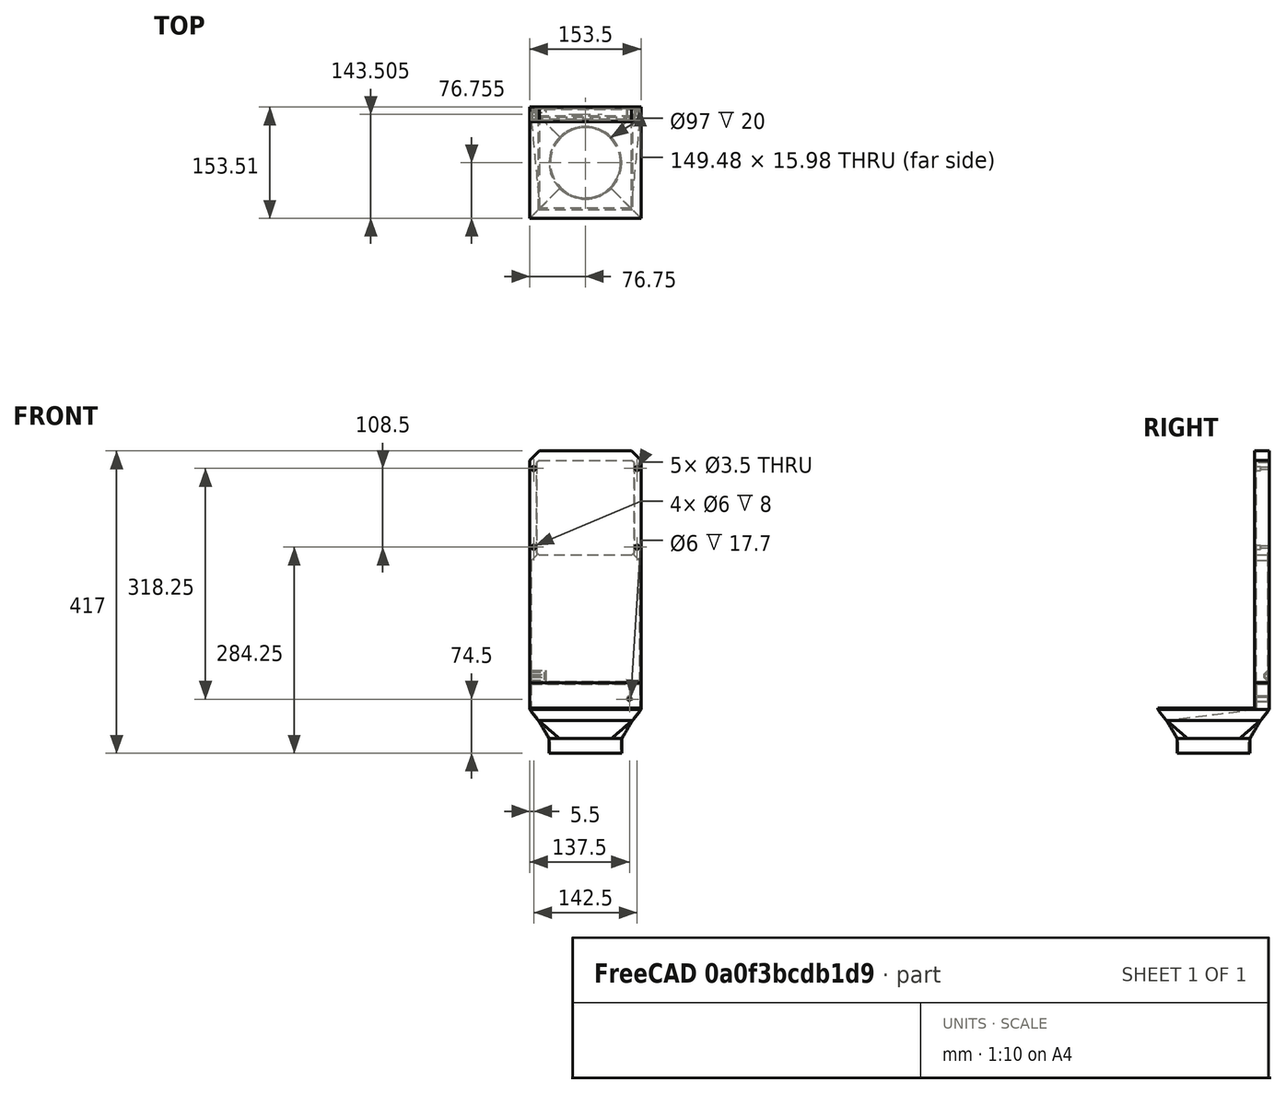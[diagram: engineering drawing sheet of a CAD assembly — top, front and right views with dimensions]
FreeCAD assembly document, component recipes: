
FREECAD ASSEMBLY — COMPONENT RECIPES ("H2C Vertical Exhaust")

This assembly document has 2 components, labeled P0..P1 below (a component is one placed body or linked part). 2 of them carry a construction recipe — the FreeCAD feature program that regenerates the part from scratch, quoted from this document or its linked companion documents; the rest are supplied as boundary geometry only. No exploded tour is included for this assembly.
COMPONENT P0 — recipe-attached ("Back of printer001", modeled in this document).
Construction recipe (the document's own serialized feature program — sketch geometry with constraints, then the solid features built on it; lengths are millimeters unless a unit is written):

FEATURE [Sketcher::SketchObject] Sketch
  ArcFitTolerance = 1e-06
  AttachmentSupport = -> [XZ_Plane]
  ExternalTypes = [0]
  FullyConstrained = true
  MakeInternals = false
  MapMode = 5
  Placement = pos=(0,0,0) rot=(1,0,0;1.5708rad)
  sketch-geometry (25):
    g0: LineSegment StartX=-76.75 StartY=-241.5 StartZ=0 EndX=76.75 EndY=-241.5 EndZ=0
    g1: LineSegment StartX=76.75 StartY=-241.5 StartZ=0 EndX=76.75 EndY=65.5 EndZ=0
    g2: LineSegment StartX=63.75 StartY=78.5 StartZ=0 EndX=-63.75 EndY=78.5 EndZ=0
    g3: LineSegment StartX=-76.75 StartY=65.5 StartZ=0 EndX=-76.75 EndY=-241.5 EndZ=0
    g4: GeomPoint X=0 Y=0 Z=0
    g5: GeomPoint X=-76.75 Y=78.5 Z=0
    g6: GeomPoint X=76.75 Y=78.5 Z=0
    g7: LineSegment StartX=-63.75 StartY=-65.5 StartZ=0 EndX=63.75 EndY=-65.5 EndZ=0
    g8: LineSegment StartX=67.25 StartY=-62 StartZ=0 EndX=67.25 EndY=62 EndZ=0
    g9: LineSegment StartX=63.75 StartY=65.5 StartZ=0 EndX=-63.75 EndY=65.5 EndZ=0
    g10: LineSegment StartX=-67.25 StartY=62 StartZ=0 EndX=-67.25 EndY=-62 EndZ=0
    g11: GeomPoint X=0 Y=0 Z=0
    g12: GeomPoint X=-67.25 Y=65.5 Z=0
    g13: GeomPoint X=67.25 Y=65.5 Z=0
    g14: GeomPoint X=67.25 Y=-62 Z=0
    g15: Circle CenterX=-71.25 CenterY=54.25 CenterZ=0 NormalX=0 NormalY=0 NormalZ=1 AngleXU=0 Radius=1.75
    g16: Circle CenterX=71.25 CenterY=54.25 CenterZ=0 NormalX=0 NormalY=0 NormalZ=1 AngleXU=0 Radius=1.75
    g17: Circle CenterX=71.25 CenterY=-54.25 CenterZ=0 NormalX=0 NormalY=0 NormalZ=1 AngleXU=0 Radius=1.75
    g18: Circle CenterX=-71.25 CenterY=-54.25 CenterZ=0 NormalX=0 NormalY=0 NormalZ=1 AngleXU=0 Radius=1.75
    g19: LineSegment StartX=-76.75 StartY=65.5 StartZ=0 EndX=-63.75 EndY=78.5 EndZ=0
    g20: LineSegment StartX=63.75 StartY=78.5 StartZ=0 EndX=76.75 EndY=65.5 EndZ=0
    g21: LineSegment StartX=-67.25 StartY=62 StartZ=0 EndX=-63.75 EndY=65.5 EndZ=0
    g22: LineSegment StartX=63.75 StartY=65.5 StartZ=0 EndX=67.25 EndY=62 EndZ=0
    g23: LineSegment StartX=-67.25 StartY=-62 StartZ=0 EndX=-63.75 EndY=-65.5 EndZ=0
    g24: LineSegment StartX=63.75 StartY=-65.5 StartZ=0 EndX=67.25 EndY=-62 EndZ=0
  constraints (59):
    c: Horizontal(g0)
    c: Vertical(g3)
    c: Coincident(g4,g-1)
    c: DistanceX(g5,g6) = 153.5
    c: PointOnObject(g5,g3)
    c: PointOnObject(g5,g2)
    c: PointOnObject(g6,g2)
    c: PointOnObject(g6,g1)
    c: Horizontal(g7)
    c: Coincident(g11,g4)
    c: DistanceX(g12,g13) = 134.5
    c: DistanceY(g14,g13) = 127.5
    c: PointOnObject(g12,g10)
    c: PointOnObject(g12,g9)
    c: PointOnObject(g13,g9)
    c: PointOnObject(g13,g8)
    c: Horizontal(g15,g16)
    c: Horizontal(g18,g17)
    c: Vertical(g16,g17)
    c: Vertical(g15,g18)
    c: DistanceX(g15,g16) = 142.5
    c: DistanceY(g17,g16) = 108.5
    c: Symmetric(g18,g16,g4)
    c: Equal(g15,g16)
    c: Equal(g15,g18)
    c: Equal(g15,g17)
    c: Diameter(g15) = 3.5
    c: Vertical(g10)
    c: Coincident(g14,g8)
    c: Coincident(g1,g0)
    c: Coincident(g0,g3)
    c: DistanceY(g0,g2) = 320
    c: Coincident(g19,g3)
    c: Coincident(g19,g2)
    c: Coincident(g20,g2)
    c: Coincident(g20,g1)
    c: Symmetric(g2,g2,g-2)
    c: Symmetric(g3,g1,g-2)
    c: DistanceX(g3,g9) = 13
    c: Horizontal(g3,g9)
    c: Vertical(g2,g9)
    c: Coincident(g21,g10)
    c: Coincident(g21,g9)
    c: Coincident(g22,g9)
    c: Coincident(g22,g8)
    c: Angle(g19,g3) = 0.785398
    c: Angle(g21,g10) = 0.785398
    c: Symmetric(g9,g9,g-2)
    c: Symmetric(g8,g10,g-2)
    c: Vertical(g7,g9)
    c: Coincident(g23,g10)
    c: Coincident(g23,g7)
    c: Coincident(g24,g7)
    c: Coincident(g24,g8)
    c: Vertical(g7,g9)
    c: Horizontal(g10,g8)
    c: Angle(g10,g23) = 0.785398
    c: Symmetric(g8,g10,g4)
    c: Vertical(g1)
FEATURE [PartDesign::Pad] Pad  label="Surface against printer"
  Direction = (0,-1,2e-16)
  Length = 2
  Length2 = 10
  Placement = pos=(0,0,0) rot=(1,0,0;1.5708rad)
  Profile = -> Sketch
  ReferenceAxis = -> Sketch [N_Axis]
  SideType = 0
  Suppressed = false
  Type = 0
  Type2 = 0
FEATURE [Sketcher::SketchObject] Sketch011
  ArcFitTolerance = 1e-06
  AttachmentSupport = -> [Pad]
  ExternalGeometry = -> [Pad]
  ExternalTypes = [0]
  FullyConstrained = true
  MakeInternals = false
  MapMode = 5
  Placement = pos=(0,-1.17e-14,0) rot=(-1,0,0;1.5708rad)
  sketch-geometry (16):
    g0: LineSegment StartX=-76.75 StartY=-65.5 StartZ=0 EndX=-76.75 EndY=241.5 EndZ=0
    g1: LineSegment StartX=-76.75 StartY=241.5 StartZ=0 EndX=-74.75 EndY=241.5 EndZ=0
    g2: LineSegment StartX=-74.75 StartY=241.5 StartZ=0 EndX=-74.75 EndY=73 EndZ=0
    g3: LineSegment StartX=-74.75 StartY=73 StartZ=0 EndX=-67.25 EndY=65.5 EndZ=0
    g4: LineSegment StartX=-67.25 StartY=65.5 StartZ=0 EndX=-67.25 EndY=-62 EndZ=0
    g5: LineSegment StartX=-67.25 StartY=-62 StartZ=0 EndX=-63.75 EndY=-65.5 EndZ=0
    g6: LineSegment StartX=-63.75 StartY=-65.5 StartZ=0 EndX=63.75 EndY=-65.5 EndZ=0
    g7: LineSegment StartX=63.75 StartY=-65.5 StartZ=0 EndX=67.25 EndY=-62 EndZ=0
    g8: LineSegment StartX=67.25 StartY=-62 StartZ=0 EndX=67.25 EndY=65.5 EndZ=0
    g9: LineSegment StartX=67.25 StartY=65.5 StartZ=0 EndX=74.75 EndY=73 EndZ=0
    g10: LineSegment StartX=74.75 StartY=73 StartZ=0 EndX=74.75 EndY=241.5 EndZ=0
    g11: LineSegment StartX=74.75 StartY=241.5 StartZ=0 EndX=76.75 EndY=241.5 EndZ=0
    g12: LineSegment StartX=76.75 StartY=241.5 StartZ=0 EndX=76.75 EndY=-65.5 EndZ=0
    g13: LineSegment StartX=76.75 StartY=-65.5 StartZ=0 EndX=63.75 EndY=-78.5 EndZ=0
    g14: LineSegment StartX=63.75 StartY=-78.5 StartZ=0 EndX=-63.75 EndY=-78.5 EndZ=0
    g15: LineSegment StartX=-63.75 StartY=-78.5 StartZ=0 EndX=-76.75 EndY=-65.5 EndZ=0
  constraints (38):
    c: Coincident(g-6,g0)
    c: Coincident(g0,g-7)
    c: Coincident(g0,g1)
    c: PointOnObject(g1,g-7)
    c: Coincident(g1,g2)
    c: Vertical(g2)
    c: Coincident(g2,g3)
    c: Coincident(g3,g4)
    c: Coincident(g4,g-3)
    c: PointOnObject(g-3,g4)
    c: DistanceX(g1,g1) = 2
    c: Angle(g2,g3) = 0.785398
    c: PointOnObject(g3,g-8)
    c: Coincident(g4,g5)
    c: Coincident(g5,g-9)
    c: Coincident(g5,g6)
    c: Coincident(g6,g-9)
    c: Coincident(g6,g7)
    c: Coincident(g7,g-4)
    c: Coincident(g7,g8)
    c: Vertical(g8)
    c: Coincident(g8,g9)
    c: Coincident(g9,g10)
    c: PointOnObject(g10,g-7)
    c: Vertical(g10)
    c: Coincident(g10,g11)
    c: Coincident(g11,g-7)
    c: Coincident(g11,g12)
    c: Coincident(g12,g-5)
    c: Coincident(g12,g13)
    c: Coincident(g13,g-5)
    c: Coincident(g13,g14)
    c: Coincident(g14,g-6)
    c: Coincident(g14,g15)
    c: Coincident(g15,g0)
    c: Angle(g9,g10) = 0.785398
    c: PointOnObject(g8,g-8)
    c: Equal(g11,g1)
FEATURE [PartDesign::Pad] Pad006  label="Duct walls"
  BaseFeature = -> Pad
  Direction = (0,1,2e-16)
  Length = 16
  Length2 = 10
  Placement = pos=(0,0,0) rot=(1,0,0;1.5708rad)
  Profile = -> Sketch011
  ReferenceAxis = -> Sketch011 [N_Axis]
  Refine = true
  SideType = 0
  Suppressed = false
  Type = 0
  Type2 = 0
FEATURE [Sketcher::SketchObject] Sketch012
  ArcFitTolerance = 1e-06
  AttachmentSupport = -> [Pad006]
  ExternalGeometry = -> [Pad006]
  ExternalTypes = [0]
  FullyConstrained = true
  MakeInternals = false
  MapMode = 5
  Placement = pos=(0,16,0) rot=(-1,0,0;1.5708rad)
  sketch-geometry (6):
    g0: LineSegment StartX=-76.75 StartY=241.5 StartZ=0 EndX=-76.75 EndY=-65.5 EndZ=0
    g1: LineSegment StartX=-76.75 StartY=-65.5 StartZ=0 EndX=-63.75 EndY=-78.5 EndZ=0
    g2: LineSegment StartX=-63.75 StartY=-78.5 StartZ=0 EndX=63.75 EndY=-78.5 EndZ=0
    g3: LineSegment StartX=63.75 StartY=-78.5 StartZ=0 EndX=76.75 EndY=-65.5 EndZ=0
    g4: LineSegment StartX=76.75 StartY=-65.5 StartZ=0 EndX=76.75 EndY=241.5 EndZ=0
    g5: LineSegment StartX=76.75 StartY=241.5 StartZ=0 EndX=-76.75 EndY=241.5 EndZ=0
  constraints (12):
    c: Coincident(g-3,g0)
    c: Coincident(g0,g-3)
    c: Coincident(g0,g1)
    c: Coincident(g1,g-5)
    c: Coincident(g1,g2)
    c: Coincident(g2,g-5)
    c: Coincident(g2,g3)
    c: Coincident(g3,g-4)
    c: Coincident(g3,g4)
    c: Coincident(g4,g-4)
    c: Coincident(g4,g5)
    c: Coincident(g5,g0)
FEATURE [PartDesign::Pad] Pad007  label="Surface away from printer"
  BaseFeature = -> Pad006
  Direction = (0,1,2e-16)
  Length = 2
  Length2 = 10
  Placement = pos=(0,0,0) rot=(1,0,0;1.5708rad)
  Profile = -> Sketch012
  ReferenceAxis = -> Sketch012 [N_Axis]
  Refine = true
  SideType = 0
  Suppressed = false
  Type = 0
  Type2 = 0
FEATURE [Sketcher::SketchObject] Sketch003
  ArcFitTolerance = 1e-06
  AttachmentOffset = pos=(0,0,6) rot=(0,0,1;0rad)
  AttachmentSupport = -> [Pad007]
  ExternalTypes = [0]
  FullyConstrained = true
  MakeInternals = false
  MapMode = 5
  Placement = pos=(0,10,1.3e-15) rot=(1,0,0;1.5708rad)
  sketch-geometry (4):
    g0: Circle CenterX=71.25 CenterY=54.25 CenterZ=0 NormalX=0 NormalY=0 NormalZ=1 AngleXU=0 Radius=3
    g1: Circle CenterX=-71.25 CenterY=54.25 CenterZ=0 NormalX=0 NormalY=0 NormalZ=1 AngleXU=0 Radius=3
    g2: Circle CenterX=-71.25 CenterY=-54.25 CenterZ=0 NormalX=0 NormalY=0 NormalZ=1 AngleXU=0 Radius=3
    g3: Circle CenterX=71.25 CenterY=-54.25 CenterZ=0 NormalX=0 NormalY=0 NormalZ=1 AngleXU=0 Radius=3
  constraints (8):
    c: Coincident(g0,g-4)
    c: Coincident(g1,g-3)
    c: Coincident(g2,g-6)
    c: Coincident(g3,g-5)
    c: Equal(g3,g2)
    c: Equal(g0,g1)
    c: Equal(g1,g2)
    c: Diameter(g3) = 6
FEATURE [PartDesign::Pocket] Pocket  label="Screw head pockets"
  BaseFeature = -> Pad007
  Direction = (0,1,-2e-16)
  Length = 5
  Length2 = 5
  Placement = pos=(0,0,0) rot=(1,0,0;1.5708rad)
  Profile = -> Sketch003
  ReferenceAxis = -> Sketch003 [N_Axis]
  SideType = 0
  Suppressed = false
  Type = 1
  Type2 = 0
FEATURE [PartDesign::Pocket] Pocket001  label="Screw pockets"
  BaseFeature = -> Pocket
  Direction = (0,-1,0)
  Length = 5
  Length2 = 5
  Placement = pos=(0,0,0) rot=(1,0,0;1.5708rad)
  Profile = -> Pocket [Edge44,Edge45,Edge46,Edge43]
  Reversed = true
  SideType = 0
  Suppressed = false
  Type = 1
  Type2 = 0
FEATURE [Sketcher::SketchObject] Sketch013
  ArcFitTolerance = 1e-06
  AttachmentSupport = -> [Pocket001]
  ExternalGeometry = -> [Pocket001]
  ExternalTypes = [0]
  FullyConstrained = true
  MakeInternals = false
  MapMode = 5
  Placement = pos=(76.75,0,0) rot=(0.707107,0,0.707107;3.14159rad)
  sketch-geometry (7):
    g0: LineSegment StartX=-239.5 StartY=2 StartZ=0 EndX=-239.5 EndY=1.572e-13 EndZ=0
    g1: LineSegment StartX=-239.5 StartY=1.572e-13 StartZ=0 EndX=-234 EndY=-5.5 EndZ=0
    g2: LineSegment StartX=-234 StartY=-5.5 StartZ=0 EndX=-230 EndY=-5.5 EndZ=0
    g3: LineSegment StartX=-230 StartY=-5.5 StartZ=0 EndX=-224.5 EndY=1.572e-13 EndZ=0
    g4: LineSegment StartX=-224.5 StartY=1.572e-13 StartZ=0 EndX=-224.5 EndY=2 EndZ=0
    g5: LineSegment StartX=-224.5 StartY=2 StartZ=0 EndX=-239.5 EndY=2 EndZ=0
    g6: GeomPoint X=-54.25 Y=2 Z=0
  constraints (19):
    c: PointOnObject(g0,g-4)
    c: Vertical(g0)
    c: Coincident(g0,g1)
    c: Coincident(g1,g2)
    c: Horizontal(g2)
    c: Coincident(g2,g3)
    c: Coincident(g3,g4)
    c: PointOnObject(g4,g-4)
    c: Vertical(g4)
    c: Coincident(g4,g5)
    c: Coincident(g5,g0)
    c: Angle(g0,g1) = 0.785398
    c: Angle(g3,g4) = 0.785398
    c: DistanceX(g5,g5) = 15
    c: DistanceY(g2,g4) = 7.5
    c: DistanceY(g4,g4) = 2
    c: Symmetric(g-3,g-3,g6)
    c: Horizontal(g0,g3)
    c: DistanceX(g4,g6) = 170.25
FEATURE [PartDesign::Pad] Pad008  label="Filament tube walls"
  BaseFeature = -> Pocket001
  Direction = (1,0,-2e-16)
  Length = 22
  Length2 = 10
  Placement = pos=(0,0,0) rot=(1,0,0;1.5708rad)
  Profile = -> Sketch013
  ReferenceAxis = -> Sketch013 [N_Axis]
  Refine = true
  Reversed = true
  SideType = 0
  Suppressed = false
  Type = 0
  Type2 = 0
FEATURE [Sketcher::SketchObject] Sketch014
  ArcFitTolerance = 1e-06
  AttachmentSupport = -> [Pad008]
  ExternalGeometry = -> [Sketch013]
  ExternalTypes = [0]
  FullyConstrained = true
  MakeInternals = false
  MapMode = 5
  Placement = pos=(76.75,0,0) rot=(0.707107,0,0.707107;3.14159rad)
  sketch-geometry (7):
    g0: LineSegment StartX=-237.5 StartY=2 StartZ=0 EndX=-237.5 EndY=0.828427 EndZ=0
    g1: LineSegment StartX=-237.5 StartY=0.828427 StartZ=0 EndX=-233.172 EndY=-3.5 EndZ=0
    g2: LineSegment StartX=-233.172 StartY=-3.5 StartZ=0 EndX=-230.828 EndY=-3.5 EndZ=0
    g3: LineSegment StartX=-230.828 StartY=-3.5 StartZ=0 EndX=-226.5 EndY=0.828427 EndZ=0
    g4: LineSegment StartX=-226.5 StartY=0.828427 StartZ=0 EndX=-226.5 EndY=2 EndZ=0
    g5: LineSegment StartX=-226.5 StartY=2 StartZ=0 EndX=-237.5 EndY=2 EndZ=0
    g6: LineSegment StartX=-230 StartY=-5.5 StartZ=0 EndX=-230.828 EndY=-3.5 EndZ=0
  constraints (20):
    c: PointOnObject(g0,g-3)
    c: Vertical(g0)
    c: Coincident(g0,g1)
    c: Coincident(g1,g2)
    c: Horizontal(g2)
    c: Coincident(g2,g3)
    c: Coincident(g3,g4)
    c: PointOnObject(g4,g-3)
    c: Vertical(g4)
    c: Coincident(g4,g5)
    c: Coincident(g5,g0)
    c: Angle(g0,g1) = 0.785398
    c: Angle(g3,g4) = 0.785398
    c: DistanceX(g-3,g0) = 2
    c: DistanceX(g4,g-3) = 2
    c: DistanceY(g-4,g2) = 2
    c: Horizontal(g0,g3)
    c: Coincident(g6,g-4)
    c: Coincident(g6,g2)
    c: Angle(g6,g-4) = 1.1781
FEATURE [PartDesign::Pocket] Pocket002  label="Filament tube opening"
  BaseFeature = -> Pad008
  Direction = (-1,0,2e-16)
  Length = 20
  Length2 = 5
  Placement = pos=(0,0,0) rot=(1,0,0;1.5708rad)
  Profile = -> Sketch014 [Edge3,Edge2,Edge1,Edge7,Edge6,Edge5]
  ReferenceAxis = -> Sketch014 [N_Axis]
  SideType = 0
  Suppressed = false
  Type = 0
  Type2 = 0
FEATURE [PartDesign::Body] Body  label="Back of printer"
  AllowCompound = false
  Group = -> [Sketch,Pad,Pad006,Pad007,Pocket,Pocket001,Sketch003,Sketch011,Sketch012,Sketch013,Pad008,Sketch014,Pocket002]
  Origin = -> Origin
  Placement = pos=(2e-15,15.975,0) rot=(0,0,1;3.14159rad)
  Tip = -> Pocket002
COMPONENT P1 — recipe-attached ("Duct adapter001", modeled in this document).
Construction recipe (the document's own serialized feature program — sketch geometry with constraints, then the solid features built on it; lengths are millimeters unless a unit is written):

FEATURE [PartDesign::SubShapeBinder] Binder  label="Duct opening binder"
  BindCopyOnChange = 0
  BindMode = 0
  ClaimChildren = false
  Context = -> Body001 [Binder.]
  Fuse = false
  MakeFace = true
  OffsetFill = false
  OffsetIntersection = false
  OffsetJoinType = 0
  OffsetOpenResult = false
  PartialLoad = false
  Relative = true
  Support = -> [Body[Pocket002.Face3]]
  _Version = 2
FEATURE [PartDesign::Plane] DatumPlane  label="Duct opening plane"
  AttachmentSupport = -> [Binder]
  Length = 184.895
  MapMode = 13
  Placement = pos=(25.5833,4.64167,-241.5) rot=(0,0,1;0rad)
  ResizeMode = 0
  Width = 191.92
FEATURE [Sketcher::SketchObject] Sketch015
  ArcFitTolerance = 1e-06
  AttachmentSupport = -> [DatumPlane]
  ExternalGeometry = -> [Binder]
  ExternalTypes = [0]
  FullyConstrained = true
  MakeInternals = false
  MapMode = 5
  Placement = pos=(25.5833,4.64167,-241.5) rot=(0,0,1;0rad)
  sketch-geometry (8):
    g0: LineSegment StartX=49.1667 StartY=-4.66667 StartZ=0 EndX=49.1667 EndY=11.3333 EndZ=0
    g1: LineSegment StartX=49.1667 StartY=11.3333 StartZ=0 EndX=-100.333 EndY=11.3333 EndZ=0
    g2: LineSegment StartX=-100.333 StartY=11.3333 StartZ=0 EndX=-100.333 EndY=-4.66667 EndZ=0
    g3: LineSegment StartX=-100.333 StartY=-4.66667 StartZ=0 EndX=49.1667 EndY=-4.66667 EndZ=0
    g4: LineSegment StartX=51.1667 StartY=-6.66667 StartZ=0 EndX=51.1667 EndY=13.3333 EndZ=0
    g5: LineSegment StartX=51.1667 StartY=13.3333 StartZ=0 EndX=-102.333 EndY=13.3333 EndZ=0
    g6: LineSegment StartX=-102.333 StartY=13.3333 StartZ=0 EndX=-102.333 EndY=-6.66667 EndZ=0
    g7: LineSegment StartX=-102.333 StartY=-6.66667 StartZ=0 EndX=51.1667 EndY=-6.66667 EndZ=0
  constraints (20):
    c: Coincident(g0,g1)
    c: Coincident(g1,g2)
    c: Coincident(g2,g3)
    c: Coincident(g3,g0)
    c: Vertical(g0)
    c: Vertical(g2)
    c: Horizontal(g1)
    c: Horizontal(g3)
    c: Coincident(g0,g-4)
    c: Coincident(g1,g-5)
    c: Coincident(g4,g5)
    c: Coincident(g5,g6)
    c: Coincident(g6,g7)
    c: Coincident(g7,g4)
    c: Vertical(g4)
    c: Vertical(g6)
    c: Horizontal(g5)
    c: Horizontal(g7)
    c: Coincident(g4,g-3)
    c: Coincident(g5,g-6)
FEATURE [PartDesign::Pad] Pad009  label="Tube extension to top of printer"
  Direction = (0,-4.3e-15,1)
  Length = 35
  Length2 = 10
  Placement = pos=(25.5833,4.64167,-241.5) rot=(0,0,1;0rad)
  Profile = -> Sketch015
  ReferenceAxis = -> Sketch015 [N_Axis]
  Reversed = true
  SideType = 0
  Suppressed = false
  Type = 0
  Type2 = 0
FEATURE [Sketcher::SketchObject] Sketch016
  ArcFitTolerance = 1e-06
  AttachmentSupport = -> [Pad009]
  ExternalGeometry = -> [Pad009]
  ExternalTypes = [0]
  FullyConstrained = true
  MakeInternals = false
  MapMode = 5
  Placement = pos=(25.5833,4.64167,-241.5) rot=(0,0,1;0rad)
  sketch-geometry (9):
    g0: LineSegment StartX=49.1667 StartY=-4.66667 StartZ=0 EndX=49.1667 EndY=11.3333 EndZ=0
    g1: LineSegment StartX=49.1667 StartY=11.3333 StartZ=0 EndX=-100.333 EndY=11.3333 EndZ=0
    g2: LineSegment StartX=-100.333 StartY=11.3333 StartZ=0 EndX=-100.333 EndY=-4.66667 EndZ=0
    g3: LineSegment StartX=-100.333 StartY=-4.66667 StartZ=0 EndX=49.1667 EndY=-4.66667 EndZ=0
    g4: LineSegment StartX=47.6667 StartY=-3.16667 StartZ=0 EndX=47.6667 EndY=9.83333 EndZ=0
    g5: LineSegment StartX=47.6667 StartY=9.83333 StartZ=0 EndX=-98.8333 EndY=9.83333 EndZ=0
    g6: LineSegment StartX=-98.8333 StartY=9.83333 StartZ=0 EndX=-98.8333 EndY=-3.16667 EndZ=0
    g7: LineSegment StartX=-98.8333 StartY=-3.16667 StartZ=0 EndX=47.6667 EndY=-3.16667 EndZ=0
    g8: GeomPoint X=-25.5833 Y=3.33333 Z=0
  constraints (22):
    c: Coincident(g0,g1)
    c: Coincident(g1,g2)
    c: Coincident(g2,g3)
    c: Coincident(g3,g0)
    c: Vertical(g0)
    c: Vertical(g2)
    c: Horizontal(g1)
    c: Horizontal(g3)
    c: Coincident(g0,g-3)
    c: Coincident(g1,g-4)
    c: Coincident(g4,g5)
    c: Coincident(g5,g6)
    c: Coincident(g6,g7)
    c: Coincident(g7,g4)
    c: Vertical(g4)
    c: Vertical(g6)
    c: Horizontal(g5)
    c: Horizontal(g7)
    c: Symmetric(g0,g1,g8)
    c: Symmetric(g4,g5,g8)
    c: DistanceX(g1,g5) = 1.5
    c: DistanceY(g5,g1) = 1.5
FEATURE [PartDesign::Pad] Pad010  label="Connector"
  BaseFeature = -> Pad009
  Direction = (0,-8.9e-15,1)
  Length = 4
  Length2 = 10
  Placement = pos=(25.5833,4.64167,-241.5) rot=(0,0,1;0rad)
  Profile = -> Sketch016
  ReferenceAxis = -> Sketch016 [N_Axis]
  SideType = 2
  Suppressed = false
  Type = 0
  Type2 = 0
FEATURE [PartDesign::Chamfer] Chamfer  label="Connector chamfer 1"
  Angle = 45
  Base = -> Pad010 [Edge28,Edge22,Edge27,Edge25]
  BaseFeature = -> Pad010
  ChamferType = 0
  FlipDirection = false
  Placement = pos=(25.5833,4.64167,-241.5) rot=(0,0,1;0rad)
  Size = 0.75
  Size2 = 1
  SupportTransform = false
  Suppressed = false
  UseAllEdges = false
FEATURE [PartDesign::Chamfer] Chamfer001  label="Connector chamfer 2"
  Angle = 45
  Base = -> Chamfer [Edge43,Edge44,Edge39,Edge41]
  BaseFeature = -> Chamfer
  ChamferType = 0
  FlipDirection = false
  Placement = pos=(25.5833,4.64167,-241.5) rot=(0,0,1;0rad)
  Size = 1.49
  Size2 = 1
  SupportTransform = false
  Suppressed = false
  UseAllEdges = false
FEATURE [Sketcher::SketchObject] Sketch017
  ArcFitTolerance = 1e-06
  AttachmentSupport = -> [Chamfer001]
  ExternalGeometry = -> [Chamfer001]
  ExternalTypes = [0]
  FullyConstrained = true
  MakeInternals = false
  MapMode = 5
  Placement = pos=(25.5833,4.64167,-276.5) rot=(1,0,0;3.14159rad)
  sketch-geometry (8):
    g0: LineSegment StartX=49.1667 StartY=-11.3333 StartZ=0 EndX=49.1667 EndY=4.66667 EndZ=0
    g1: LineSegment StartX=49.1667 StartY=4.66667 StartZ=0 EndX=-100.333 EndY=4.66667 EndZ=0
    g2: LineSegment StartX=-100.333 StartY=4.66667 StartZ=0 EndX=-100.333 EndY=-11.3333 EndZ=0
    g3: LineSegment StartX=-100.333 StartY=-11.3333 StartZ=0 EndX=49.1667 EndY=-11.3333 EndZ=0
    g4: LineSegment StartX=51.1667 StartY=-13.3333 StartZ=0 EndX=51.1667 EndY=140.167 EndZ=0
    g5: LineSegment StartX=51.1667 StartY=140.167 StartZ=0 EndX=-102.333 EndY=140.167 EndZ=0
    g6: LineSegment StartX=-102.333 StartY=140.167 StartZ=0 EndX=-102.333 EndY=-13.3333 EndZ=0
    g7: LineSegment StartX=-102.333 StartY=-13.3333 StartZ=0 EndX=51.1667 EndY=-13.3333 EndZ=0
  constraints (20):
    c: Coincident(g0,g1)
    c: Coincident(g1,g2)
    c: Coincident(g2,g3)
    c: Coincident(g3,g0)
    c: Vertical(g0)
    c: Vertical(g2)
    c: Horizontal(g1)
    c: Horizontal(g3)
    c: Coincident(g0,g-5)
    c: Coincident(g1,g-6)
    c: Coincident(g4,g5)
    c: Coincident(g5,g6)
    c: Coincident(g6,g7)
    c: Coincident(g7,g4)
    c: Vertical(g4)
    c: Vertical(g6)
    c: Horizontal(g5)
    c: Coincident(g4,g-3)
    c: Coincident(g6,g-4)
    c: Equal(g4,g7)
FEATURE [PartDesign::Pad] Pad011  label="Surface against top of printer"
  BaseFeature = -> Chamfer001
  Direction = (0,1.32e-14,-1)
  Length = 2
  Length2 = 10
  Placement = pos=(25.5833,4.64167,-241.5) rot=(0,0,1;0rad)
  Profile = -> Sketch017
  ReferenceAxis = -> Sketch017 [N_Axis]
  SideType = 0
  Suppressed = false
  Type = 0
  Type2 = 0
FEATURE [Sketcher::SketchObject] Sketch018
  ArcFitTolerance = 1e-06
  AttachmentOffset = pos=(0,0,40) rot=(0,0,1;0rad)
  AttachmentSupport = -> [Pad011]
  ExternalGeometry = -> [Pad011]
  ExternalTypes = [0]
  FullyConstrained = true
  MakeInternals = false
  MapMode = 5
  Placement = pos=(25.5833,4.64167,-318.5) rot=(1,0,0;3.14159rad)
  expr: Constraints[3] = VarSet.Diameter - 3 mm
  expr: Constraints[4] = VarSet.Diameter
  sketch-geometry (3):
    g0: GeomPoint X=-25.5833 Y=63.4167 Z=0
    g1: Circle CenterX=-25.5833 CenterY=63.4167 CenterZ=0 NormalX=0 NormalY=0 NormalZ=1 AngleXU=0 Radius=50
    g2: Circle CenterX=-25.5833 CenterY=63.4167 CenterZ=0 NormalX=0 NormalY=0 NormalZ=1 AngleXU=0 Radius=48.5
  constraints (5):
    c: Symmetric(g-3,g-4,g0)
    c: Coincident(g1,g0)
    c: Coincident(g2,g0)
    c: Diameter(g2) = 97
    c: Diameter(g1) = 100
FEATURE [Sketcher::SketchObject] Sketch019
  ArcFitTolerance = 1e-06
  AttachmentOffset = pos=(0,0,15) rot=(0,0,1;0rad)
  AttachmentSupport = -> [Pad011]
  ExternalGeometry = -> [Pad011]
  ExternalTypes = [0]
  FullyConstrained = true
  MakeInternals = false
  MapMode = 5
  Placement = pos=(25.5833,4.64167,-293.5) rot=(1,0,0;3.14159rad)
  sketch-geometry (11):
    g0: GeomPoint X=-25.5833 Y=63.4167 Z=0
    g1: LineSegment StartX=-90.5833 StartY=-1.58333 StartZ=0 EndX=39.4167 EndY=-1.58333 EndZ=0
    g2: LineSegment StartX=39.4167 StartY=-1.58333 StartZ=0 EndX=39.4167 EndY=128.417 EndZ=0
    g3: LineSegment StartX=39.4167 StartY=128.417 StartZ=0 EndX=-90.5833 EndY=128.417 EndZ=0
    g4: LineSegment StartX=-90.5833 StartY=128.417 StartZ=0 EndX=-90.5833 EndY=-1.58333 EndZ=0
    g5: GeomPoint X=-25.5833 Y=63.4167 Z=0
    g6: LineSegment StartX=-88.5833 StartY=0.416667 StartZ=0 EndX=37.4167 EndY=0.416667 EndZ=0
    g7: LineSegment StartX=37.4167 StartY=0.416667 StartZ=0 EndX=37.4167 EndY=126.417 EndZ=0
    g8: LineSegment StartX=37.4167 StartY=126.417 StartZ=0 EndX=-88.5833 EndY=126.417 EndZ=0
    g9: LineSegment StartX=-88.5833 StartY=126.417 StartZ=0 EndX=-88.5833 EndY=0.416667 EndZ=0
    g10: GeomPoint X=-25.5833 Y=63.4167 Z=0
  constraints (25):
    c: Symmetric(g-3,g-4,g0)
    c: Coincident(g1,g2)
    c: Coincident(g2,g3)
    c: Coincident(g3,g4)
    c: Coincident(g4,g1)
    c: Horizontal(g1)
    c: Horizontal(g3)
    c: Vertical(g2)
    c: Vertical(g4)
    c: Symmetric(g3,g1,g5)
    c: Coincident(g5,g0)
    c: DistanceY(g2,g2) = 130
    c: Equal(g1,g2)
    c: Coincident(g6,g7)
    c: Coincident(g7,g8)
    c: Coincident(g8,g9)
    c: Coincident(g9,g6)
    c: Horizontal(g6)
    c: Horizontal(g8)
    c: Vertical(g7)
    c: Vertical(g9)
    c: Symmetric(g8,g6,g10)
    c: Coincident(g10,g0)
    c: Equal(g7,g6)
    c: DistanceY(g8,g3) = 2
FEATURE [PartDesign::AdditiveLoft] AdditiveLoft  label="Transition to larger square opening"
  BaseFeature = -> Pad011
  Closed = false
  Placement = pos=(25.5833,4.64167,-241.5) rot=(0,0,1;0rad)
  Profile = -> Pad011 [Face28]
  Ruled = false
  Sections = -> [Sketch019]
  Suppressed = false
FEATURE [PartDesign::AdditiveLoft] AdditiveLoft001  label="Transition to circle"
  BaseFeature = -> AdditiveLoft
  Closed = false
  Placement = pos=(25.5833,4.64167,-241.5) rot=(0,0,1;0rad)
  Profile = -> AdditiveLoft [Face36]
  Ruled = false
  Sections = -> [Sketch018]
  Suppressed = false
FEATURE [PartDesign::Pad] Pad012  label="Interface with duct"
  BaseFeature = -> AdditiveLoft001
  Direction = (0,1.77e-14,-1)
  Length = 20
  Length2 = 10
  Placement = pos=(25.5833,4.64167,-241.5) rot=(0,0,1;0rad)
  Profile = -> Sketch018
  ReferenceAxis = -> Sketch018 [N_Axis]
  Refine = true
  SideType = 0
  Suppressed = false
  Type = 0
  Type2 = 0
FEATURE [Sketcher::SketchObject] Sketch020
  ArcFitTolerance = 1e-06
  AttachmentSupport = -> [Pad012]
  ExternalTypes = [0]
  FullyConstrained = true
  MakeInternals = false
  MapMode = 5
  Placement = pos=(25.5833,-2.025,-241.5) rot=(1,0,0;1.5708rad)
  sketch-geometry (1):
    g0: Circle CenterX=35.1667 CenterY=-22.5 CenterZ=0 NormalX=0 NormalY=0 NormalZ=1 AngleXU=0 Radius=4
  constraints (3):
    c: DistanceX(g0,g-3) = 16
    c: Diameter(g0) = 8
    c: DistanceY(g-3,g0) = 12.5
FEATURE [PartDesign::Pad] Pad013  label="Screw column"
  BaseFeature = -> Pad012
  Direction = (0,-1,-3e-14)
  Length = 10
  Length2 = 10
  Placement = pos=(25.5833,4.64167,-241.5) rot=(0,0,1;0rad)
  Profile = -> Sketch020
  ReferenceAxis = -> Sketch020 [N_Axis]
  Refine = true
  Reversed = true
  SideType = 0
  Suppressed = false
  Type = 3
  Type2 = 0
  UpToFace = -> Pad012 [Face49]
FEATURE [Sketcher::SketchObject] Sketch021
  ArcFitTolerance = 1e-06
  AttachmentSupport = -> [Pad013]
  ExternalGeometry = -> [Sketch020]
  ExternalTypes = [0]
  FullyConstrained = true
  MakeInternals = false
  MapMode = 5
  Placement = pos=(25.5833,-2.025,-241.5) rot=(1,0,0;1.5708rad)
  sketch-geometry (1):
    g0: Circle CenterX=35.1667 CenterY=-22.5 CenterZ=0 NormalX=0 NormalY=0 NormalZ=1 AngleXU=0 Radius=1.75
  constraints (2):
    c: Coincident(g0,g-3)
    c: Diameter(g0) = 3.5
FEATURE [PartDesign::Pocket] Pocket003  label="Screw tunnel"
  BaseFeature = -> Pad013
  Direction = (0,1,3.4e-14)
  Length = 5
  Length2 = 5
  Placement = pos=(25.5833,4.64167,-241.5) rot=(0,0,1;0rad)
  Profile = -> Sketch021
  ReferenceAxis = -> Sketch021 [N_Axis]
  SideType = 0
  Suppressed = false
  Type = 1
  Type2 = 0
FEATURE [Sketcher::SketchObject] Sketch022
  ArcFitTolerance = 1e-06
  AttachmentSupport = -> [Pocket003]
  ExternalGeometry = -> [Pocket003]
  ExternalTypes = [0]
  FullyConstrained = true
  MakeInternals = false
  MapMode = 5
  Placement = pos=(25.5833,17.975,-241.5) rot=(0,0.707107,0.707107;3.14159rad)
  sketch-geometry (1):
    g0: Circle CenterX=-35.1667 CenterY=-22.5 CenterZ=0 NormalX=0 NormalY=0 NormalZ=1 AngleXU=0 Radius=3
  constraints (2):
    c: Coincident(g0,g-3)
    c: Diameter(g0) = 6
FEATURE [PartDesign::Pocket] Pocket004  label="Screw head recess"
  BaseFeature = -> Pocket003
  Direction = (0,-1,-3.85e-14)
  Length = 17.7
  Length2 = 5
  Placement = pos=(25.5833,4.64167,-241.5) rot=(0,0,1;0rad)
  Profile = -> Sketch022
  ReferenceAxis = -> Sketch022 [N_Axis]
  SideType = 0
  Suppressed = false
  Type = 0
  Type2 = 0
FEATURE [App::VarSet] VarSet
  Diameter = 100
FEATURE [PartDesign::Body] Body001  label="Duct adapter"
  AllowCompound = false
  Group = -> [Binder,DatumPlane,Sketch015,Pad009,Sketch016,Pad010,Chamfer,Chamfer001,Sketch017,Pad011,Sketch019,AdditiveLoft,Sketch018,AdditiveLoft001,Pad012,Sketch020,Pad013,Sketch021,Pocket003,Sketch022,Pocket004,VarSet]
  Origin = -> Origin001
  Tip = -> Pocket004
PROVENANCE & LICENSES
A FreeCAD (.FCStd) document from a public repository crawl; recipes are the document's own serialized feature recipes (and, for linked parts, companion documents' recipes).
License: other.
